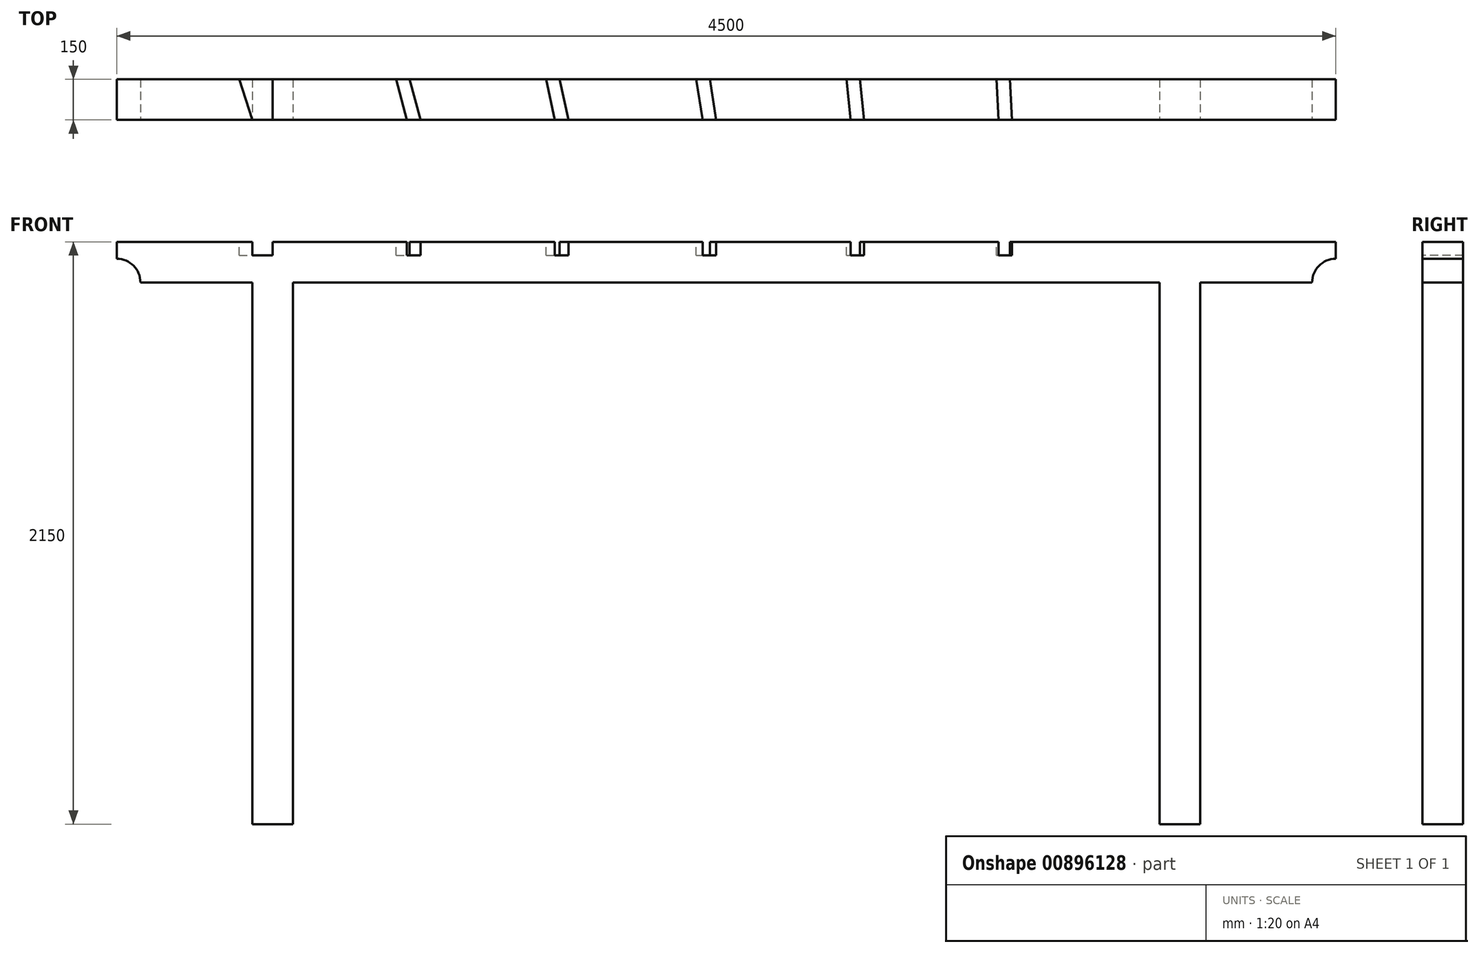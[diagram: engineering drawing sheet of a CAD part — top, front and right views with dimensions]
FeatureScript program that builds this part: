
annotation { "Feature Type Name" : "Feature", "Feature Type Description" : "" }
export const myFeature = defineFeature(function(context is Context, id is Id, definition is map)
    precondition{}
    {
        {
            var Q0;
            Q0=qCreatedBy(makeId("Front.planeOp"),FACE);
            var sketch = newSketch(context, id + "F0", { "sketchPlane" : qUnion([Q0])});
            skLineSegment(sketch, "E0.bottom", {"start": v(0, 0) * mm, "end": v(150, 0) * mm});
            skLineSegment(sketch, "E0.top", {"start": v(0, 2000) * mm, "end": v(150, 2000) * mm});
            skLineSegment(sketch, "E0.left", {"start": v(0, 0) * mm, "end": v(0, 2000) * mm});
            skLineSegment(sketch, "E0.right", {"start": v(150, 0) * mm, "end": v(150, 2000) * mm});
            skLineSegment(sketch, "E1.bottom", {"start": v(150, 2000) * mm, "end": v(650, 2000) * mm});
            skLineSegment(sketch, "E1.top", {"start": v(150, 2150) * mm, "end": v(650, 2150) * mm});
            skLineSegment(sketch, "E1.left", {"start": v(150, 2000) * mm, "end": v(150, 2150) * mm});
            skLineSegment(sketch, "E1.right", {"start": v(650, 2000) * mm, "end": v(650, 2150) * mm});
            skLineSegment(sketch, "E2.bottom", {"start": v(150, 2000) * mm, "end": v(-3350, 2000) * mm});
            skLineSegment(sketch, "E2.top", {"start": v(150, 2150) * mm, "end": v(-3350, 2150) * mm});
            skLineSegment(sketch, "E2.right", {"start": v(-3350, 2000) * mm, "end": v(-3350, 2150) * mm});
            skLineSegment(sketch, "E3.bottom", {"start": v(-3350, 2000) * mm, "end": v(-3200, 2000) * mm});
            skLineSegment(sketch, "E3.top", {"start": v(-3350, 0) * mm, "end": v(-3200, 0) * mm});
            skLineSegment(sketch, "E3.left", {"start": v(-3350, 2000) * mm, "end": v(-3350, 0) * mm});
            skLineSegment(sketch, "E3.right", {"start": v(-3200, 2000) * mm, "end": v(-3200, 0) * mm});
            skLineSegment(sketch, "E4.bottom", {"start": v(-3350, 2000) * mm, "end": v(-3850, 2000) * mm});
            skLineSegment(sketch, "E4.top", {"start": v(-3350, 2150) * mm, "end": v(-3850, 2150) * mm});
            skLineSegment(sketch, "E4.right", {"start": v(-3850, 2000) * mm, "end": v(-3850, 2150) * mm});
            skSolve(sketch);
        }
        {
            var Q0;
            Q0 = qSketchRegion(id + "F0", true);
            extrude(context, id + "F1", {"entities" : qUnion([Q0]), "oppositeDirection" : true, "depth" : 150 * mm, "offsetDistance" : 25 * mm});
        }
        {
            var Q0;
            Q0=sQuery(id+"F0.wireOp",VERTEX,"E4.bottom.end");
            var Q1;
            Q1=makeQuery(id+"F1.opExtrude","SWEPT_BODY",BODY,{"disambiguationData":[OSD([sQuery(id+"F0.wireOp",EDGE,"E0.bottom"),sQuery(id+"F0.wireOp",EDGE,"E0.left"),sQuery(id+"F0.wireOp",EDGE,"E0.right"),sQuery(id+"F0.wireOp",EDGE,"E1.bottom"),sQuery(id+"F0.wireOp",EDGE,"E1.top"),sQuery(id+"F0.wireOp",EDGE,"E1.right"),sQuery(id+"F0.wireOp",EDGE,"E2.bottom"),sQuery(id+"F0.wireOp",EDGE,"E2.top"),sQuery(id+"F0.wireOp",EDGE,"E3.top"),sQuery(id+"F0.wireOp",EDGE,"E3.left"),sQuery(id+"F0.wireOp",EDGE,"E3.right"),sQuery(id+"F0.wireOp",EDGE,"E4.bottom"),sQuery(id+"F0.wireOp",EDGE,"E4.top"),sQuery(id+"F0.wireOp",EDGE,"E4.right")])]});
            hole(context, id + "F2", {"style" : HoleStyle.SIMPLE, "endStyle" : HoleEndStyle.THROUGH, "holeDiameter" : 175 * mm, "majorDiameter" : 5 * mm, "isTappedThrough" : true, "tappedDepth" : 12 * mm, "tapClearance" : 3, "locations" : qUnion([Q0]), "scope" : qUnion([Q1])});
        }
        {
            var Q0;
            Q0=sQuery(id+"F0.wireOp",VERTEX,"E1.bottom.end");
            var Q1;
            Q1=makeQuery(id+"F1.opExtrude","SWEPT_BODY",BODY,{"disambiguationData":[OSD([sQuery(id+"F0.wireOp",EDGE,"E0.bottom"),sQuery(id+"F0.wireOp",EDGE,"E0.left"),sQuery(id+"F0.wireOp",EDGE,"E0.right"),sQuery(id+"F0.wireOp",EDGE,"E1.bottom"),sQuery(id+"F0.wireOp",EDGE,"E1.top"),sQuery(id+"F0.wireOp",EDGE,"E1.right"),sQuery(id+"F0.wireOp",EDGE,"E2.bottom"),sQuery(id+"F0.wireOp",EDGE,"E2.top"),sQuery(id+"F0.wireOp",EDGE,"E3.top"),sQuery(id+"F0.wireOp",EDGE,"E3.left"),sQuery(id+"F0.wireOp",EDGE,"E3.right"),sQuery(id+"F0.wireOp",EDGE,"E4.bottom"),sQuery(id+"F0.wireOp",EDGE,"E4.top"),sQuery(id+"F0.wireOp",EDGE,"E4.right")])]});
            hole(context, id + "F3", {"style" : HoleStyle.SIMPLE, "endStyle" : HoleEndStyle.THROUGH, "holeDiameter" : 175 * mm, "majorDiameter" : 5 * mm, "isTappedThrough" : true, "tappedDepth" : 12 * mm, "tapClearance" : 3, "locations" : qUnion([Q0]), "scope" : qUnion([Q1])});
        }
        {
            var Q0;
            Q0=makeQuery(id+"F1.opExtrude","SWEPT_FACE",FACE,{"disambiguationData":[OSD([sQuery(id+"F0.wireOp",EDGE,"E1.top"),sQuery(id+"F0.wireOp",EDGE,"E2.top"),sQuery(id+"F0.wireOp",EDGE,"E4.top")])]});
            var sketch = newSketch(context, id + "F4", { "sketchPlane" : qUnion([Q0])});
            skLineSegment(sketch, "E5", {"start": v(-3850, 0) * mm, "end": v(-3850, 150) * mm});
            skLineSegment(sketch, "E6", {"start": v(-3850, 150) * mm, "end": v(-3898, 150) * mm});
            skLineSegment(sketch, "E7", {"start": v(-3898, 150) * mm, "end": v(-3850, 0) * mm});
            skLineSegment(sketch, "E8.1.0.0", {"start": v(-3350, 0) * mm, "end": v(-3350, 150) * mm});
            skLineSegment(sketch, "E8.1.0.1", {"start": v(-3350, 150) * mm, "end": v(-3398, 150) * mm});
            skLineSegment(sketch, "E8.1.0.2", {"start": v(-3398, 150) * mm, "end": v(-3350, 0) * mm});
            skLineSegment(sketch, "E8.direction1", {"start": v(-3850, 0) * mm, "end": v(-3350, 0) * mm, "construction": true});
            skLineSegment(sketch, "E9.1.0.0", {"start": v(-3200, 0) * mm, "end": v(-3200, 150) * mm});
            skLineSegment(sketch, "E9.1.0.1", {"start": v(-3200, 150) * mm, "end": v(-3248, 150) * mm});
            skLineSegment(sketch, "E9.1.0.2", {"start": v(-3248, 150) * mm, "end": v(-3200, 0) * mm});
            skLineSegment(sketch, "E9.direction1", {"start": v(-3350, 0) * mm, "end": v(-3200, 0) * mm, "construction": true});
            skLineSegment(sketch, "E10", {"start": v(-3350, 0) * mm, "end": v(-3398, 150) * mm});
            skLineSegment(sketch, "E11", {"start": v(-3350, 0) * mm, "end": v(-3200, 0) * mm});
            skLineSegment(sketch, "E12", {"start": v(-3248, 150) * mm, "end": v(-3398, 150) * mm});
            skLineSegment(sketch, "E13", {"start": v(-3275, 0) * mm, "end": v(-3275, 330.56) * mm});
            skLineSegment(sketch, "E14.1.0.0", {"start": v(-2729, 0) * mm, "end": v(-2729, 330.56) * mm});
            skLineSegment(sketch, "E14.2.0.0", {"start": v(-2183, 0) * mm, "end": v(-2183, 330.56) * mm});
            skLineSegment(sketch, "E14.3.0.0", {"start": v(-1637, 0) * mm, "end": v(-1637, 330.56) * mm});
            skLineSegment(sketch, "E14.4.0.0", {"start": v(-1091, 0) * mm, "end": v(-1091, 330.56) * mm});
            skLineSegment(sketch, "E14.5.0.0", {"start": v(-545, 0) * mm, "end": v(-545, 330.56) * mm});
            skLineSegment(sketch, "E14.direction1", {"start": v(-3275, 0) * mm, "end": v(-2729, 0) * mm, "construction": true});
            skLineSegment(sketch, "E15", {"start": v(-2729, 330.56) * mm, "end": v(-2817, 330.56) * mm});
            skLineSegment(sketch, "E16", {"start": v(-2183, 330.56) * mm, "end": v(-2253.5, 330.56) * mm});
            skLineSegment(sketch, "E17", {"start": v(-1637, 330.56) * mm, "end": v(-1690, 330.56) * mm});
            skLineSegment(sketch, "E18", {"start": v(-1091, 330.56) * mm, "end": v(-1126, 330.56) * mm});
            skLineSegment(sketch, "E19", {"start": v(-545, 330.56) * mm, "end": v(-562.6, 330.56) * mm});
            skLineSegment(sketch, "E20", {"start": v(-2817, 330.56) * mm, "end": v(-2729, 0) * mm});
            skLineSegment(sketch, "E21", {"start": v(-2253.5, 330.56) * mm, "end": v(-2183, 0) * mm});
            skLineSegment(sketch, "E22", {"start": v(-1690, 330.56) * mm, "end": v(-1637, 0) * mm});
            skLineSegment(sketch, "E23", {"start": v(-1126, 330.56) * mm, "end": v(-1091, 0) * mm});
            skLineSegment(sketch, "E24", {"start": v(-562.6, 330.56) * mm, "end": v(-545, 0) * mm});
            skLineSegment(sketch, "E25.1.0.0", {"start": v(-2867, 330.56) * mm, "end": v(-2779, 0) * mm});
            skLineSegment(sketch, "E25.direction1", {"start": v(-2729, 0) * mm, "end": v(-2779, 0) * mm, "construction": true});
            skLineSegment(sketch, "E26.1.0.0", {"start": v(-2303.5, 330.56) * mm, "end": v(-2233, 0) * mm});
            skLineSegment(sketch, "E26.direction1", {"start": v(-2183, 0) * mm, "end": v(-2233, 0) * mm, "construction": true});
            skLineSegment(sketch, "E27.1.0.0", {"start": v(-1740, 330.56) * mm, "end": v(-1687, 0) * mm});
            skLineSegment(sketch, "E27.direction1", {"start": v(-1637, 0) * mm, "end": v(-1687, 0) * mm, "construction": true});
            skLineSegment(sketch, "E28.1.0.0", {"start": v(-1176, 330.56) * mm, "end": v(-1141, 0) * mm});
            skLineSegment(sketch, "E28.direction1", {"start": v(-1091, 0) * mm, "end": v(-1141, 0) * mm, "construction": true});
            skLineSegment(sketch, "E29.1.0.0", {"start": v(-612.6, 330.56) * mm, "end": v(-595, 0) * mm});
            skLineSegment(sketch, "E29.direction1", {"start": v(-545, 0) * mm, "end": v(-595, 0) * mm, "construction": true});
            skLineSegment(sketch, "E30", {"start": v(-2867, 330.56) * mm, "end": v(-2817, 330.56) * mm});
            skLineSegment(sketch, "E31", {"start": v(-2729, 0) * mm, "end": v(-2779, 0) * mm});
            skLineSegment(sketch, "E32", {"start": v(-2303.5, 330.56) * mm, "end": v(-2253.5, 330.56) * mm});
            skLineSegment(sketch, "E33", {"start": v(-2183, 0) * mm, "end": v(-2233, 0) * mm});
            skLineSegment(sketch, "E34", {"start": v(-1687, 0) * mm, "end": v(-1637, 0) * mm});
            skLineSegment(sketch, "E35", {"start": v(-1740, 330.56) * mm, "end": v(-1690, 330.56) * mm});
            skLineSegment(sketch, "E36", {"start": v(-1176, 330.56) * mm, "end": v(-1126, 330.56) * mm});
            skLineSegment(sketch, "E37", {"start": v(-1091, 0) * mm, "end": v(-1141, 0) * mm});
            skLineSegment(sketch, "E38", {"start": v(-612.6, 330.56) * mm, "end": v(-562.6, 330.56) * mm});
            skLineSegment(sketch, "E39", {"start": v(-545, 0) * mm, "end": v(-595, 0) * mm});
            skLineSegment(sketch, "E40", {"start": v(-2818.93, 150) * mm, "end": v(-2768.93, 150) * mm});
            skLineSegment(sketch, "E41", {"start": v(-2265, 150) * mm, "end": v(-2215, 150) * mm});
            skLineSegment(sketch, "E42", {"start": v(-1711.05, 150) * mm, "end": v(-1661.05, 150) * mm});
            skLineSegment(sketch, "E43", {"start": v(-1156.88, 150) * mm, "end": v(-1106.88, 150) * mm});
            skLineSegment(sketch, "E44", {"start": v(-602.99, 150) * mm, "end": v(-552.99, 150) * mm});
            skSolve(sketch);
        }
        {
            var Q0;
            {var subQ0=sQuery(id+"F4.wireOp",EDGE,"E8.1.0.0");Q0=makeQuery(id+"F4.imprint","IMPRINT",FACE,{"disambiguationData":[TD([[makeQuery(id+"F4.imprint","IMPRINT",EDGE,{"derivedFrom":subQ0}),1.0]])]});}
            var Q1;
            {var subQ0=sQuery(id+"F4.wireOp",EDGE,"E8.1.0.0");Q1=makeQuery(id+"F4.imprint","IMPRINT",FACE,{"disambiguationData":[TD([[makeQuery(id+"F4.imprint","IMPRINT",EDGE,{"derivedFrom":subQ0}),-1.0]])]});}
            extrude(context, id + "F5", {"entities" : qUnion([Q0, Q1]), "operationType" : NewBodyOperationType.REMOVE, "oppositeDirection" : true, "depth" : 50 * mm, "offsetDistance" : 25 * mm});
        }
        {
            var Q0;
            {var subQ0=sQuery(id+"F4.wireOp",EDGE,"E31");Q0=makeQuery(id+"F4.imprint","IMPRINT",FACE,{"disambiguationData":[TD([[makeQuery(id+"F4.imprint","IMPRINT",EDGE,{"derivedFrom":subQ0}),1.0]])]});}
            extrude(context, id + "F6", {"entities" : qUnion([Q0]), "operationType" : NewBodyOperationType.REMOVE, "oppositeDirection" : true, "depth" : 50 * mm, "offsetDistance" : 25 * mm});
        }
        {
            var Q0;
            {var subQ0=sQuery(id+"F4.wireOp",EDGE,"E39");Q0=makeQuery(id+"F4.imprint","IMPRINT",FACE,{"disambiguationData":[TD([[makeQuery(id+"F4.imprint","IMPRINT",EDGE,{"derivedFrom":subQ0}),1.0]])]});}
            var Q1;
            {var subQ0=sQuery(id+"F4.wireOp",EDGE,"E37");Q1=makeQuery(id+"F4.imprint","IMPRINT",FACE,{"disambiguationData":[TD([[makeQuery(id+"F4.imprint","IMPRINT",EDGE,{"derivedFrom":subQ0}),1.0]])]});}
            var Q2;
            {var subQ0=sQuery(id+"F4.wireOp",EDGE,"E34");Q2=makeQuery(id+"F4.imprint","IMPRINT",FACE,{"disambiguationData":[TD([[makeQuery(id+"F4.imprint","IMPRINT",EDGE,{"derivedFrom":subQ0}),1.0]])]});}
            var Q3;
            {var subQ0=sQuery(id+"F4.wireOp",EDGE,"E33");Q3=makeQuery(id+"F4.imprint","IMPRINT",FACE,{"disambiguationData":[TD([[makeQuery(id+"F4.imprint","IMPRINT",EDGE,{"derivedFrom":subQ0}),1.0]])]});}
            extrude(context, id + "F7", {"entities" : qUnion([Q0, Q1, Q2, Q3]), "operationType" : NewBodyOperationType.REMOVE, "oppositeDirection" : true, "depth" : 50 * mm, "offsetDistance" : 25 * mm});
        }
    });
